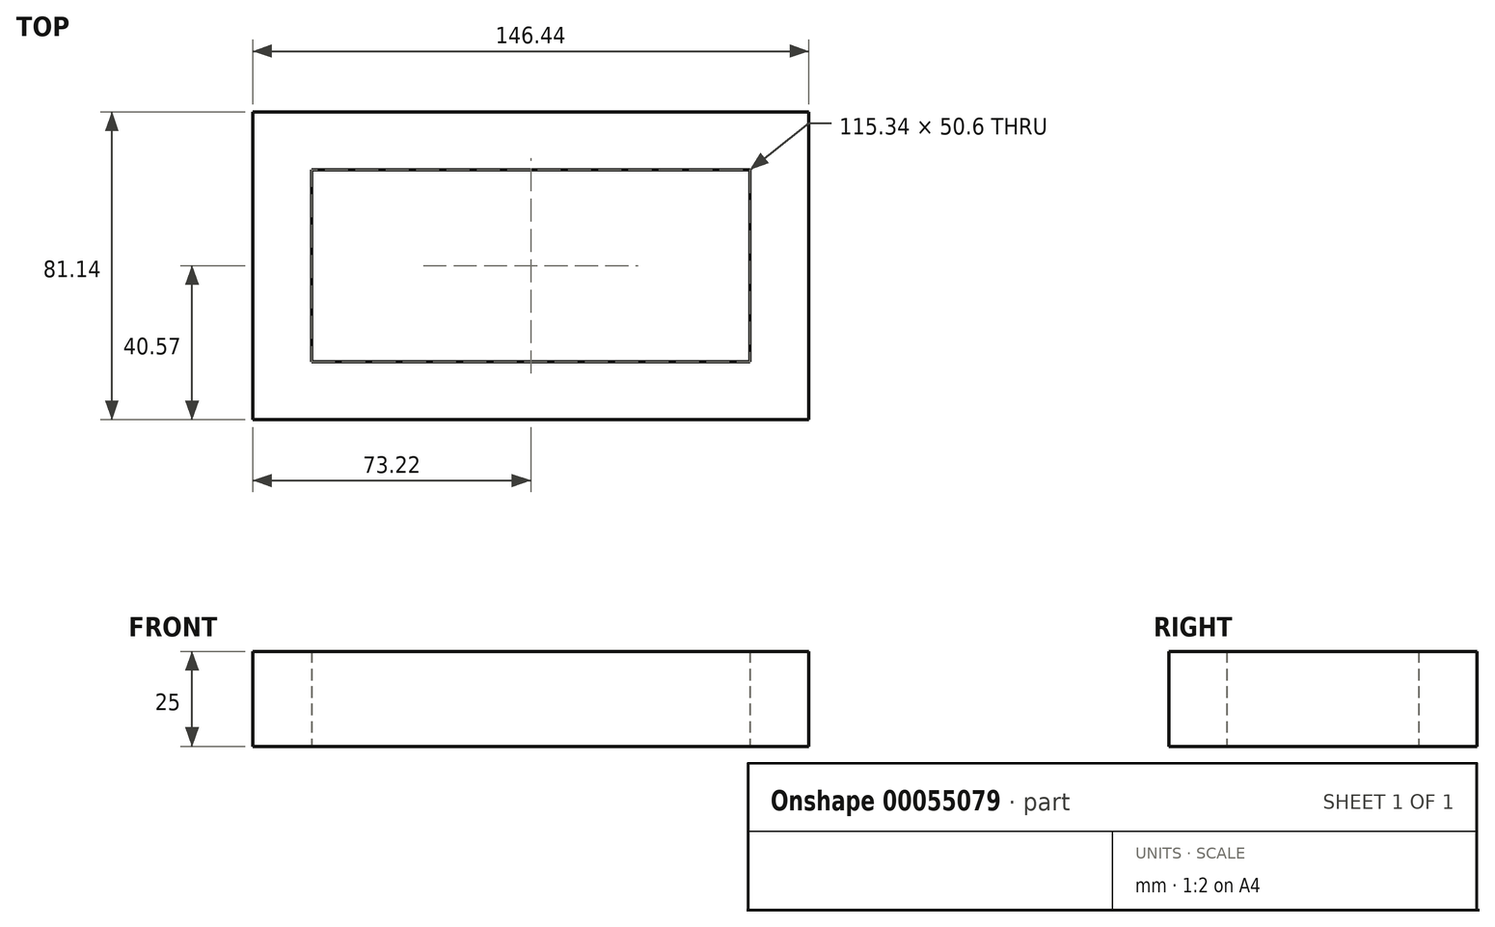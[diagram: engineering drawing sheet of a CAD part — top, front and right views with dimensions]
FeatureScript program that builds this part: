
annotation { "Feature Type Name" : "Feature", "Feature Type Description" : "" }
export const myFeature = defineFeature(function(context is Context, id is Id, definition is map)
    precondition{}
    {
        {
            var Q0;
            Q0=qCreatedBy(makeId("Top.planeOp"),FACE);
            var sketch = newSketch(context, id + "F0", { "sketchPlane" : qUnion([Q0])});
            skLineSegment(sketch, "E0.rect.bottom", {"start": v(57.67, 25.3) * mm, "end": v(-57.67, 25.3) * mm});
            skLineSegment(sketch, "E0.rect.top", {"start": v(57.67, -25.3) * mm, "end": v(-57.67, -25.3) * mm});
            skLineSegment(sketch, "E0.rect.left", {"start": v(57.67, 25.3) * mm, "end": v(57.67, -25.3) * mm});
            skLineSegment(sketch, "E0.rect.right", {"start": v(-57.67, 25.3) * mm, "end": v(-57.67, -25.3) * mm});
            skPoint(sketch, "E0.rect.middle", {"position": v(0, 0) * mm});
            skLineSegment(sketch, "E1.rect.bottom", {"start": v(73.22, 40.57) * mm, "end": v(-73.22, 40.57) * mm});
            skLineSegment(sketch, "E1.rect.top", {"start": v(73.22, -40.57) * mm, "end": v(-73.22, -40.57) * mm});
            skLineSegment(sketch, "E1.rect.left", {"start": v(73.22, 40.57) * mm, "end": v(73.22, -40.57) * mm});
            skLineSegment(sketch, "E1.rect.right", {"start": v(-73.22, 40.57) * mm, "end": v(-73.22, -40.57) * mm});
            skSolve(sketch);
        }
        {
            var Q0;
            Q0=makeQuery(id+"F0.imprint","IMPRINT",FACE,{"disambiguationData":[TD([[makeQuery(id+"F0.imprint","IMPRINT",EDGE,{"derivedFrom":sQuery(id+"F0.wireOp",EDGE,"E0.rect.bottom")}),-1.0]])]});
            extrude(context, id + "F1", {"entities" : qUnion([Q0]), "depth" : 25 * mm});
        }
    });
